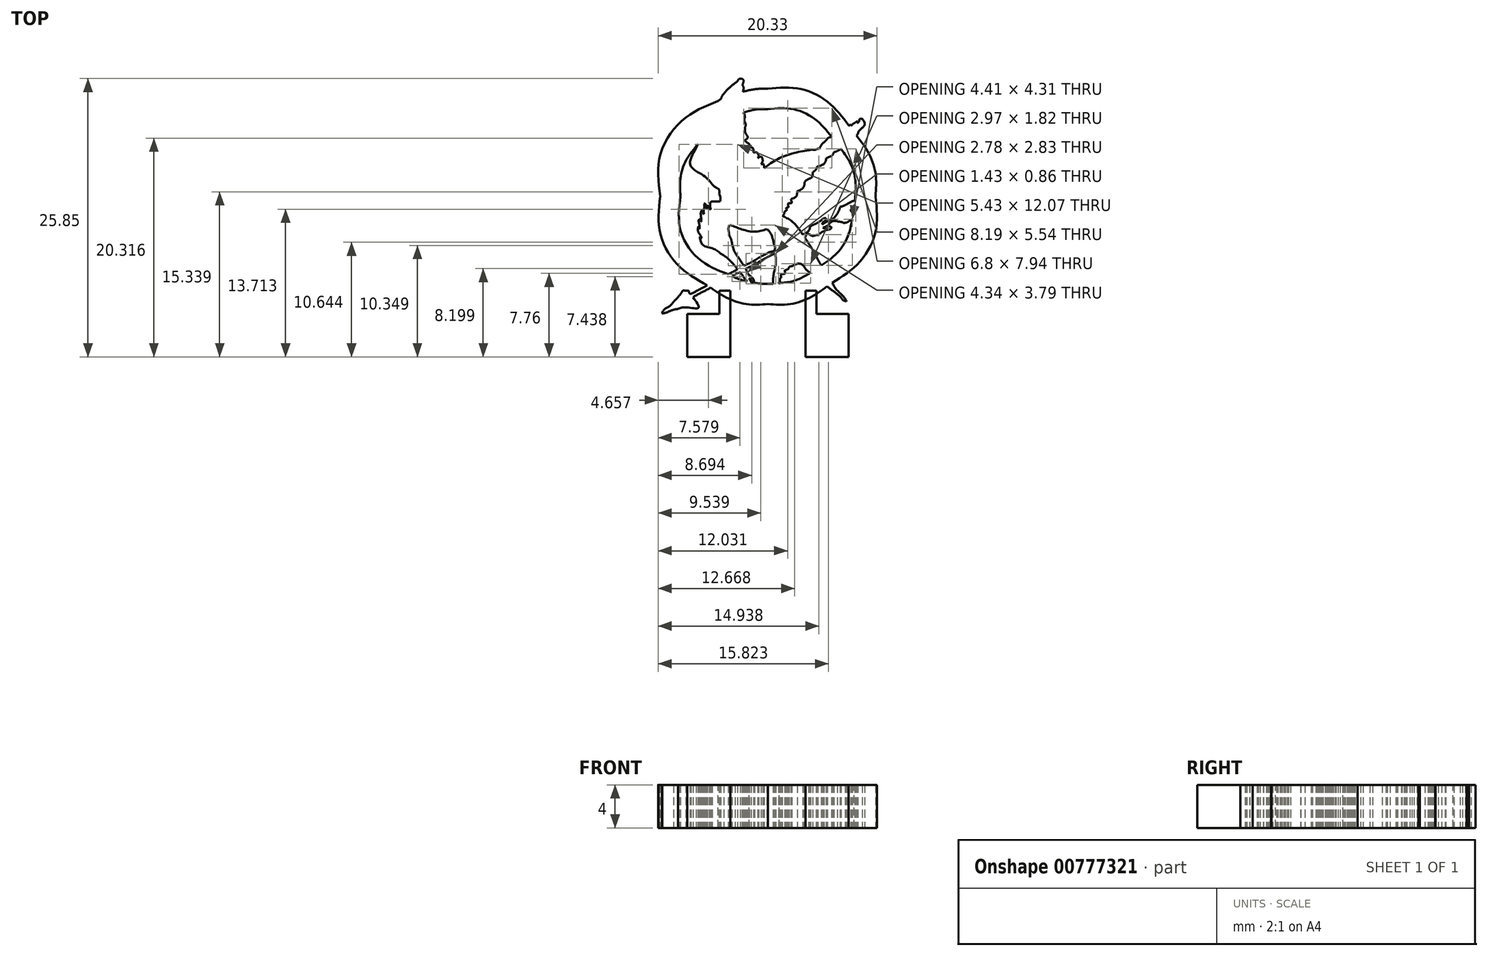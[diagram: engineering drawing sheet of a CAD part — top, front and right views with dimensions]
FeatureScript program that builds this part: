
annotation { "Feature Type Name" : "Feature", "Feature Type Description" : "" }
export const myFeature = defineFeature(function(context is Context, id is Id, definition is map)
    precondition{}
    {
        {
            var Q0;
            Q0=qCreatedBy(makeId("Top.planeOp"),FACE);
            var sketch = newSketch(context, id + "F0", { "sketchPlane" : qUnion([Q0])});
            skFitSpline(sketch, "E0", {"points": [v(6.8, 4.37) * mm, v(7.63, 3.1) * mm, v(8.11, 1.58) * mm, v(8.11, -0.04) * mm]});
            skFitSpline(sketch, "E1", {"points": [v(8.11, -0.04) * mm, v(8.11, -0.15) * mm, v(8.11, -0.27) * mm, v(8.1, -0.38) * mm]});
            skFitSpline(sketch, "E2", {"points": [v(8.08, -0.82) * mm, v(8.06, -1.02) * mm, v(8.03, -1.22) * mm, v(8, -1.41) * mm]});
            skFitSpline(sketch, "E3", {"points": [v(7.84, -2.14) * mm, v(7.37, -3.87) * mm, v(6.35, -5.38) * mm, v(4.97, -6.45) * mm]});
            skFitSpline(sketch, "E4", {"points": [v(5.98, -8.05) * mm, v(8.42, -6.23) * mm, v(10, -3.32) * mm, v(10, -0.04) * mm]});
            skFitSpline(sketch, "E5", {"points": [v(10, -0.04) * mm, v(10, 2.06) * mm, v(9.35, 4) * mm, v(8.24, 5.62) * mm]});
            skFitSpline(sketch, "E6", {"points": [v(3.96, -7.12) * mm, v(3.06, -7.62) * mm, v(2.06, -7.96) * mm, v(1, -8.1) * mm]});
            skFitSpline(sketch, "E7", {"points": [v(0.47, -8.14) * mm, v(0.31, -8.15) * mm, v(0.16, -8.16) * mm, v(0, -8.16) * mm]});
            skFitSpline(sketch, "E8", {"points": [v(0, -8.16) * mm, v(-0.42, -8.16) * mm, v(-0.84, -8.12) * mm, v(-1.25, -8.06) * mm]});
            skFitSpline(sketch, "E9", {"points": [v(-1.32, -8.05) * mm, v(-1.4, -8.03) * mm, v(-1.48, -8.02) * mm, v(-1.56, -8) * mm]});
            skFitSpline(sketch, "E10", {"points": [v(-1.9, -7.93) * mm, v(-2.4, -7.81) * mm, v(-2.87, -7.65) * mm, v(-3.33, -7.44) * mm]});
            skFitSpline(sketch, "E11", {"points": [v(-5.28, -8.5) * mm, v(-5.29, -8.5) * mm, v(-5.3, -8.5) * mm, v(-5.3, -8.51) * mm]});
            skFitSpline(sketch, "E12", {"points": [v(-5.3, -8.51) * mm, v(-3.77, -9.48) * mm, v(-1.95, -10.04) * mm, v(0, -10.04) * mm]});
            skFitSpline(sketch, "E13", {"points": [v(0, -10.04) * mm, v(2.03, -10.04) * mm, v(3.92, -9.43) * mm, v(5.5, -8.39) * mm]});
            skFitSpline(sketch, "E14", {"points": [v(-3.7, -7.26) * mm, v(-6.32, -5.92) * mm, v(-8.11, -3.19) * mm, v(-8.11, -0.04) * mm]});
            skFitSpline(sketch, "E15", {"points": [v(-8.11, -0.04) * mm, v(-8.11, 1.78) * mm, v(-7.51, 3.45) * mm, v(-6.5, 4.8) * mm]});
            skFitSpline(sketch, "E16", {"points": [v(-4.63, 8.82) * mm, v(-7.82, 7.15) * mm, v(-10, 3.8) * mm, v(-10, -0.04) * mm]});
            skFitSpline(sketch, "E17", {"points": [v(-10, -0.04) * mm, v(-10, -3.47) * mm, v(-8.27, -6.5) * mm, v(-5.63, -8.3) * mm]});
            skFitSpline(sketch, "E18", {"points": [v(-2.25, 7.75) * mm, v(-1.54, 7.96) * mm, v(-0.78, 8.07) * mm, v(0, 8.07) * mm]});
            skFitSpline(sketch, "E19", {"points": [v(0, 8.07) * mm, v(2.34, 8.07) * mm, v(4.45, 7.08) * mm, v(5.94, 5.48) * mm]});
            skFitSpline(sketch, "E20", {"points": [v(7.52, 6.54) * mm, v(5.69, 8.63) * mm, v(3, 9.96) * mm, v(0, 9.96) * mm]});
            skFitSpline(sketch, "E21", {"points": [v(0, 9.96) * mm, v(-0.8, 9.96) * mm, v(-1.57, 9.86) * mm, v(-2.31, 9.69) * mm]});
            skFitSpline(sketch, "E22", {"points": [v(-3.62, -3.38) * mm, v(-3.67, -3.09) * mm, v(-3.61, -2.8) * mm, v(-3.43, -2.7) * mm]});
            skFitSpline(sketch, "E23", {"points": [v(-3.43, -2.7) * mm, v(-2.55, -3.05) * mm, v(-1.27, -3.3) * mm, v(-0.1, -3.08) * mm]});
            skFitSpline(sketch, "E24", {"points": [v(-0.1, -3.08) * mm, v(0.21, -3.38) * mm, v(0.4, -3.81) * mm, v(0.54, -4.38) * mm]});
            skFitSpline(sketch, "E25", {"points": [v(0.54, -4.38) * mm, v(0.58, -4.53) * mm, v(0.68, -4.8) * mm, v(0.64, -4.92) * mm]});
            skFitSpline(sketch, "E26", {"points": [v(0.64, -4.92) * mm, v(0.58, -5.08) * mm, v(0.12, -5.22) * mm, v(-0.07, -5.32) * mm]});
            skFitSpline(sketch, "E27", {"points": [v(-0.07, -5.32) * mm, v(-0.77, -5.7) * mm, v(-1.6, -6.18) * mm, v(-2.25, -6.48) * mm]});
            skFitSpline(sketch, "E28", {"points": [v(-2.25, -6.48) * mm, v(-2.6, -5.92) * mm, v(-3.14, -5.07) * mm, v(-3.36, -4.24) * mm]});
            skFitSpline(sketch, "E29", {"points": [v(-3.36, -4.24) * mm, v(-3.44, -3.94) * mm, v(-3.59, -3.63) * mm, v(-3.62, -3.38) * mm]});
            skFitSpline(sketch, "E30", {"points": [v(8, -1.41) * mm, v(7.9, -1.43) * mm, v(7.8, -1.44) * mm, v(7.76, -1.44) * mm]});
            skFitSpline(sketch, "E31", {"points": [v(7.76, -1.44) * mm, v(7.73, -1.41) * mm, v(7.75, -1.33) * mm, v(7.69, -1.33) * mm]});
            skFitSpline(sketch, "E32", {"points": [v(7.69, -1.33) * mm, v(7.79, -1.13) * mm, v(7.93, -0.97) * mm, v(8.08, -0.82) * mm]});
            skFitSpline(sketch, "E33", {"points": [v(8.1, -0.38) * mm, v(7.64, -0.59) * mm, v(7.2, -0.83) * mm, v(6.72, -1.02) * mm]});
            skFitSpline(sketch, "E34", {"points": [v(6.72, -1.02) * mm, v(6.57, -1.41) * mm, v(6.37, -1.75) * mm, v(6.13, -2.06) * mm]});
            skFitSpline(sketch, "E35", {"points": [v(6.13, -2.06) * mm, v(5.76, -2.24) * mm, v(5.4, -2.42) * mm, v(5.06, -2.63) * mm]});
            skFitSpline(sketch, "E36", {"points": [v(5.06, -2.63) * mm, v(5.1, -2.45) * mm, v(5.35, -2.28) * mm, v(5.42, -2.06) * mm]});
            skFitSpline(sketch, "E37", {"points": [v(5.42, -2.06) * mm, v(5.14, -2.1) * mm, v(4.9, -2.31) * mm, v(4.64, -2.46) * mm]});
            skFitSpline(sketch, "E38", {"points": [v(4.64, -2.46) * mm, v(4.38, -2.6) * mm, v(4.1, -2.73) * mm, v(3.88, -2.91) * mm]});
            skFitSpline(sketch, "E39", {"points": [v(3.88, -2.91) * mm, v(3.88, -3.08) * mm, v(3.8, -3.15) * mm, v(3.78, -3.29) * mm]});
            skFitSpline(sketch, "E40", {"points": [v(3.78, -3.29) * mm, v(3.6, -3.39) * mm, v(3.43, -3.49) * mm, v(3.24, -3.57) * mm]});
            skFitSpline(sketch, "E41", {"points": [v(3.24, -3.57) * mm, v(2.74, -2.87) * mm, v(2.13, -2.27) * mm, v(1.35, -1.85) * mm]});
            skFitSpline(sketch, "E42", {"points": [v(1.35, -1.85) * mm, v(1.49, -1.7) * mm, v(1.55, -1.48) * mm, v(1.7, -1.35) * mm]});
            skFitSpline(sketch, "E43", {"points": [v(1.7, -1.35) * mm, v(1.74, -1.3) * mm, v(1.73, -1.2) * mm, v(1.68, -1.18) * mm]});
            skFitSpline(sketch, "E44", {"points": [v(1.68, -1.18) * mm, v(1.73, -1.1) * mm, v(1.85, -1.07) * mm, v(1.92, -1) * mm]});
            skFitSpline(sketch, "E45", {"points": [v(1.92, -1) * mm, v(1.9, -0.67) * mm, v(2.19, -0.65) * mm, v(2.13, -0.28) * mm]});
            skFitSpline(sketch, "E46", {"points": [v(2.13, -0.28) * mm, v(2.45, -0.16) * mm, v(2.67, 0.06) * mm, v(2.72, 0.45) * mm]});
            skFitSpline(sketch, "E47", {"points": [v(2.72, 0.45) * mm, v(3.1, 0.6) * mm, v(3.34, 0.9) * mm, v(3.43, 1.35) * mm]});
            skFitSpline(sketch, "E48", {"points": [v(3.43, 1.35) * mm, v(3.74, 1.57) * mm, v(4.1, 1.76) * mm, v(4.16, 2.23) * mm]});
            skFitSpline(sketch, "E49", {"points": [v(4.16, 2.23) * mm, v(4.35, 2.34) * mm, v(4.49, 2.5) * mm, v(4.56, 2.72) * mm]});
            skFitSpline(sketch, "E50", {"points": [v(4.56, 2.72) * mm, v(4.97, 2.86) * mm, v(5.3, 3.08) * mm, v(5.42, 3.5) * mm]});
            skFitSpline(sketch, "E51", {"points": [v(5.42, 3.5) * mm, v(5.71, 3.64) * mm, v(5.99, 3.79) * mm, v(6.13, 4.07) * mm]});
            skFitSpline(sketch, "E52", {"points": [v(6.13, 4.07) * mm, v(6.3, 4.13) * mm, v(6.58, 4.26) * mm, v(6.8, 4.37) * mm]});
            skFitSpline(sketch, "E53", {"points": [v(8.33, 5.73) * mm, v(8.55, 6.15) * mm, v(8.98, 6.6) * mm, v(8.78, 7.17) * mm]});
            skFitSpline(sketch, "E54", {"points": [v(8.78, 7.17) * mm, v(8.53, 7.15) * mm, v(8.47, 6.94) * mm, v(8.35, 6.8) * mm]});
            skFitSpline(sketch, "E55", {"points": [v(8.35, 6.8) * mm, v(8.3, 6.83) * mm, v(8.3, 6.92) * mm, v(8.19, 6.89) * mm]});
            skFitSpline(sketch, "E56", {"points": [v(8.19, 6.89) * mm, v(8.02, 6.77) * mm, v(7.85, 6.65) * mm, v(7.71, 6.5) * mm]});
            skFitSpline(sketch, "E57", {"points": [v(7.71, 6.5) * mm, v(7.7, 6.61) * mm, v(7.57, 6.56) * mm, v(7.52, 6.54) * mm]});
            skLineSegment(sketch, "E58", {"start": v(8.24, 5.62) * mm, "end": v(8.33, 5.73) * mm});
            skFitSpline(sketch, "E59", {"points": [v(5.94, 5.48) * mm, v(5.63, 5.42) * mm, v(5.43, 5.2) * mm, v(5.2, 5) * mm]});
            skFitSpline(sketch, "E60", {"points": [v(5.2, 5) * mm, v(5, 4.8) * mm, v(4.8, 4.48) * mm, v(4.56, 4.38) * mm]});
            skFitSpline(sketch, "E61", {"points": [v(4.56, 4.38) * mm, v(4.38, 4.3) * mm, v(4.08, 4.3) * mm, v(3.83, 4.26) * mm]});
            skFitSpline(sketch, "E62", {"points": [v(3.83, 4.26) * mm, v(2.27, 3.96) * mm, v(0.79, 3.37) * mm, v(-0.33, 2.6) * mm]});
            skFitSpline(sketch, "E63", {"points": [v(-0.33, 2.6) * mm, v(-0.36, 2.8) * mm, v(-0.41, 2.96) * mm, v(-0.64, 2.96) * mm]});
            skFitSpline(sketch, "E64", {"points": [v(-0.64, 2.96) * mm, v(-0.5, 3.21) * mm, v(-0.6, 3.65) * mm, v(-0.95, 3.53) * mm]});
            skFitSpline(sketch, "E65", {"points": [v(-0.95, 3.53) * mm, v(-0.87, 3.8) * mm, v(-1.1, 4.07) * mm, v(-1.33, 4.02) * mm]});
            skFitSpline(sketch, "E66", {"points": [v(-1.33, 4.02) * mm, v(-1.34, 4.3) * mm, v(-1.45, 4.5) * mm, v(-1.8, 4.45) * mm]});
            skFitSpline(sketch, "E67", {"points": [v(-1.8, 4.45) * mm, v(-1.71, 4.8) * mm, v(-1.97, 5) * mm, v(-2.13, 5.18) * mm]});
            skFitSpline(sketch, "E68", {"points": [v(-2.13, 5.18) * mm, v(-1.87, 5.47) * mm, v(-2.07, 5.84) * mm, v(-2.1, 6.2) * mm]});
            skFitSpline(sketch, "E69", {"points": [v(-2.1, 6.2) * mm, v(-2.13, 6.38) * mm, v(-2.06, 6.56) * mm, v(-2.09, 6.74) * mm]});
            skFitSpline(sketch, "E70", {"points": [v(-2.09, 6.74) * mm, v(-2.1, 6.83) * mm, v(-2.17, 6.92) * mm, v(-2.18, 7) * mm]});
            skFitSpline(sketch, "E71", {"points": [v(-2.18, 7) * mm, v(-2.2, 7.15) * mm, v(-2.14, 7.31) * mm, v(-2.16, 7.45) * mm]});
            skFitSpline(sketch, "E72", {"points": [v(-2.16, 7.45) * mm, v(-2.17, 7.58) * mm, v(-2.24, 7.66) * mm, v(-2.25, 7.75) * mm]});
            skFitSpline(sketch, "E73", {"points": [v(-2.3, 9.75) * mm, v(-2.26, 9.96) * mm, v(-2.27, 10.15) * mm, v(-2.37, 10.3) * mm]});
            skFitSpline(sketch, "E74", {"points": [v(-2.37, 10.3) * mm, v(-2.3, 10.5) * mm, v(-2.27, 10.77) * mm, v(-2.42, 10.9) * mm]});
            skFitSpline(sketch, "E75", {"points": [v(-2.42, 10.9) * mm, v(-2.68, 10.87) * mm, v(-2.84, 10.66) * mm, v(-3.03, 10.5) * mm]});
            skFitSpline(sketch, "E76", {"points": [v(-3.03, 10.5) * mm, v(-3.42, 10.2) * mm, v(-3.78, 9.86) * mm, v(-4.1, 9.5) * mm]});
            skFitSpline(sketch, "E77", {"points": [v(-4.1, 9.5) * mm, v(-4.25, 9.3) * mm, v(-4.37, 9.04) * mm, v(-4.55, 8.9) * mm]});
            skFitSpline(sketch, "E78", {"points": [v(-4.55, 8.9) * mm, v(-4.58, 8.87) * mm, v(-4.6, 8.85) * mm, v(-4.63, 8.82) * mm]});
            skFitSpline(sketch, "E79", {"points": [v(-6.5, 4.8) * mm, v(-6.55, 4.68) * mm, v(-6.64, 4.54) * mm, v(-6.67, 4.42) * mm]});
            skFitSpline(sketch, "E80", {"points": [v(-6.67, 4.42) * mm, v(-7.2, 2.85) * mm, v(-5.96, 1.89) * mm, v(-5.16, 1.1) * mm]});
            skFitSpline(sketch, "E81", {"points": [v(-5.16, 1.1) * mm, v(-4.92, 0.84) * mm, v(-4.54, 0.6) * mm, v(-4.52, 0.24) * mm]});
            skFitSpline(sketch, "E82", {"points": [v(-4.52, 0.24) * mm, v(-4.48, -0.48) * mm, v(-5.27, -0.53) * mm, v(-5.3, -1.25) * mm]});
            skFitSpline(sketch, "E83", {"points": [v(-5.3, -1.25) * mm, v(-5.44, -1.17) * mm, v(-5.45, -0.98) * mm, v(-5.61, -0.92) * mm]});
            skFitSpline(sketch, "E84", {"points": [v(-5.61, -0.92) * mm, v(-5.7, -0.94) * mm, v(-5.6, -1.07) * mm, v(-5.64, -1.18) * mm]});
            skFitSpline(sketch, "E85", {"points": [v(-5.64, -1.18) * mm, v(-5.75, -1.04) * mm, v(-5.77, -0.8) * mm, v(-5.92, -0.69) * mm]});
            skFitSpline(sketch, "E86", {"points": [v(-5.92, -0.69) * mm, v(-5.9, -1.03) * mm, v(-5.96, -1.3) * mm, v(-5.94, -1.66) * mm]});
            skFitSpline(sketch, "E87", {"points": [v(-5.94, -1.66) * mm, v(-6.05, -1.6) * mm, v(-6, -1.38) * mm, v(-6.06, -1.28) * mm]});
            skFitSpline(sketch, "E88", {"points": [v(-6.06, -1.28) * mm, v(-6.22, -1.5) * mm, v(-6.2, -2.01) * mm, v(-6.18, -2.34) * mm]});
            skFitSpline(sketch, "E89", {"points": [v(-6.18, -2.34) * mm, v(-6.2, -2.38) * mm, v(-6.23, -2.2) * mm, v(-6.23, -2.13) * mm]});
            skFitSpline(sketch, "E90", {"points": [v(-6.23, -2.13) * mm, v(-6.43, -2.24) * mm, v(-6.36, -2.65) * mm, v(-6.34, -2.91) * mm]});
            skFitSpline(sketch, "E91", {"points": [v(-6.34, -2.91) * mm, v(-6.36, -3.03) * mm, v(-6.42, -2.83) * mm, v(-6.46, -2.82) * mm]});
            skFitSpline(sketch, "E92", {"points": [v(-6.46, -2.82) * mm, v(-6.48, -3.3) * mm, v(-6.3, -3.6) * mm, v(-6.13, -3.9) * mm]});
            skFitSpline(sketch, "E93", {"points": [v(-6.13, -3.9) * mm, v(-6.2, -3.88) * mm, v(-6.24, -3.81) * mm, v(-6.32, -3.79) * mm]});
            skFitSpline(sketch, "E94", {"points": [v(-6.32, -3.79) * mm, v(-6, -4.58) * mm, v(-5.09, -4.88) * mm, v(-4.38, -5.35) * mm]});
            skFitSpline(sketch, "E95", {"points": [v(-4.38, -5.35) * mm, v(-3.75, -5.76) * mm, v(-3.27, -6.25) * mm, v(-2.82, -6.8) * mm]});
            skFitSpline(sketch, "E96", {"points": [v(-2.82, -6.8) * mm, v(-3.1, -6.96) * mm, v(-3.4, -7.11) * mm, v(-3.7, -7.26) * mm]});
            skLineSegment(sketch, "E97", {"start": v(-2.31, 9.69) * mm, "end": v(-2.3, 9.75) * mm});
            skFitSpline(sketch, "E98", {"points": [v(-5.63, -8.3) * mm, v(-6, -8.49) * mm, v(-6.75, -8.88) * mm, v(-7.13, -9.09) * mm]});
            skFitSpline(sketch, "E99", {"points": [v(-7.13, -9.09) * mm, v(-7.3, -9.02) * mm, v(-7.34, -8.8) * mm, v(-7.62, -8.8) * mm]});
            skFitSpline(sketch, "E100", {"points": [v(-7.62, -8.8) * mm, v(-7.9, -8.8) * mm, v(-8.05, -9.03) * mm, v(-8.24, -9.25) * mm]});
            skFitSpline(sketch, "E101", {"points": [v(-8.24, -9.25) * mm, v(-8.41, -9.47) * mm, v(-8.61, -9.67) * mm, v(-8.76, -9.82) * mm]});
            skFitSpline(sketch, "E102", {"points": [v(-8.76, -9.82) * mm, v(-9.17, -10.26) * mm, v(-9.6, -10.52) * mm, v(-9.85, -10.9) * mm]});
            skFitSpline(sketch, "E103", {"points": [v(-9.85, -10.9) * mm, v(-9.84, -10.9) * mm, v(-9.83, -10.9) * mm, v(-9.82, -10.9) * mm]});
            skFitSpline(sketch, "E104", {"points": [v(-9.82, -10.9) * mm, v(-9.4, -10.8) * mm, v(-8.94, -10.62) * mm, v(-8.33, -10.48) * mm]});
            skFitSpline(sketch, "E105", {"points": [v(-8.33, -10.48) * mm, v(-7.64, -10.33) * mm, v(-6.45, -10.38) * mm, v(-6.96, -9.4) * mm]});
            skFitSpline(sketch, "E106", {"points": [v(-6.96, -9.4) * mm, v(-6.42, -9.1) * mm, v(-5.86, -8.8) * mm, v(-5.3, -8.51) * mm]});
            skFitSpline(sketch, "E107", {"points": [v(-3.33, -7.44) * mm, v(-3.08, -7.31) * mm, v(-2.76, -7.15) * mm, v(-2.58, -7.07) * mm]});
            skFitSpline(sketch, "E108", {"points": [v(-2.58, -7.07) * mm, v(-2.35, -7.36) * mm, v(-2.16, -7.68) * mm, v(-1.9, -7.93) * mm]});
            skFitSpline(sketch, "E109", {"points": [v(-1.56, -8) * mm, v(-1.62, -7.89) * mm, v(-1.68, -7.77) * mm, v(-1.75, -7.67) * mm]});
            skFitSpline(sketch, "E110", {"points": [v(-1.75, -7.67) * mm, v(-1.61, -7.72) * mm, v(-1.5, -7.93) * mm, v(-1.32, -8.05) * mm]});
            skFitSpline(sketch, "E111", {"points": [v(-1.25, -8.06) * mm, v(-1.46, -7.57) * mm, v(-1.84, -7.24) * mm, v(-2.04, -6.74) * mm]});
            skFitSpline(sketch, "E112", {"points": [v(-2.04, -6.74) * mm, v(-1.1, -6.3) * mm, v(-0.25, -5.77) * mm, v(0.69, -5.32) * mm]});
            skFitSpline(sketch, "E113", {"points": [v(0.69, -5.32) * mm, v(0.72, -6.37) * mm, v(0.55, -7.2) * mm, v(0.47, -8.14) * mm]});
            skFitSpline(sketch, "E114", {"points": [v(1, -8.1) * mm, v(1.01, -8.06) * mm, v(1.03, -8.04) * mm, v(1.04, -8.02) * mm]});
            skFitSpline(sketch, "E115", {"points": [v(1.04, -8.02) * mm, v(1.13, -7.88) * mm, v(1.13, -7.67) * mm, v(1.25, -7.57) * mm]});
            skFitSpline(sketch, "E116", {"points": [v(1.25, -7.57) * mm, v(1.24, -7.24) * mm, v(1.54, -7.22) * mm, v(1.56, -6.9) * mm]});
            skFitSpline(sketch, "E117", {"points": [v(1.56, -6.9) * mm, v(1.74, -6.84) * mm, v(1.9, -6.76) * mm, v(1.96, -6.58) * mm]});
            skFitSpline(sketch, "E118", {"points": [v(1.96, -6.58) * mm, v(2.4, -6.43) * mm, v(2.85, -6.26) * mm, v(3.31, -6.46) * mm]});
            skFitSpline(sketch, "E119", {"points": [v(3.31, -6.46) * mm, v(3.47, -6.73) * mm, v(3.68, -6.96) * mm, v(3.96, -7.12) * mm]});
            skFitSpline(sketch, "E120", {"points": [v(5.54, -8.43) * mm, v(5.82, -8.66) * mm, v(6.14, -8.87) * mm, v(6.44, -9.1) * mm]});
            skFitSpline(sketch, "E121", {"points": [v(6.44, -9.1) * mm, v(6.73, -9.35) * mm, v(6.98, -9.66) * mm, v(7.3, -9.8) * mm]});
            skFitSpline(sketch, "E122", {"points": [v(7.3, -9.8) * mm, v(6.95, -9.25) * mm, v(6.38, -8.7) * mm, v(6, -8.1) * mm]});
            skLineSegment(sketch, "E123", {"start": v(6, -8.1) * mm, "end": v(5.98, -8.05) * mm});
            skFitSpline(sketch, "E124", {"points": [v(4.97, -6.45) * mm, v(4.46, -5.58) * mm, v(3.97, -4.7) * mm, v(3.43, -3.86) * mm]});
            skFitSpline(sketch, "E125", {"points": [v(3.43, -3.86) * mm, v(3.7, -3.52) * mm, v(4.07, -3.68) * mm, v(4.5, -3.62) * mm]});
            skFitSpline(sketch, "E126", {"points": [v(4.5, -3.62) * mm, v(4.72, -3.58) * mm, v(4.97, -3.38) * mm, v(5.2, -3.26) * mm]});
            skFitSpline(sketch, "E127", {"points": [v(5.2, -3.26) * mm, v(5.47, -3.14) * mm, v(5.75, -3.1) * mm, v(5.91, -2.91) * mm]});
            skFitSpline(sketch, "E128", {"points": [v(5.91, -2.91) * mm, v(5.71, -2.81) * mm, v(5.38, -2.97) * mm, v(5.11, -2.96) * mm]});
            skFitSpline(sketch, "E129", {"points": [v(5.11, -2.96) * mm, v(5.6, -2.7) * mm, v(5.94, -2.36) * mm, v(6.77, -2.41) * mm]});
            skFitSpline(sketch, "E130", {"points": [v(6.77, -2.41) * mm, v(6.9, -2.42) * mm, v(7.04, -2.5) * mm, v(7.17, -2.48) * mm]});
            skFitSpline(sketch, "E131", {"points": [v(7.17, -2.48) * mm, v(7.28, -2.47) * mm, v(7.57, -2.3) * mm, v(7.84, -2.14) * mm]});
            skLineSegment(sketch, "E132", {"start": v(5.5, -8.39) * mm, "end": v(5.54, -8.43) * mm});
            skSolve(sketch);
        }
        {
            var Q0;
            Q0=qCreatedBy(makeId("Top.planeOp"),FACE);
            var sketch = newSketch(context, id + "F1", { "sketchPlane" : qUnion([Q0])});
            skLineSegment(sketch, "E133.bottom", {"start": v(-7.5, -10.94) * mm, "end": v(-3.5, -10.94) * mm});
            skLineSegment(sketch, "E133.top", {"start": v(-7.5, -14.94) * mm, "end": v(-3.5, -14.94) * mm});
            skLineSegment(sketch, "E133.left", {"start": v(-7.5, -10.94) * mm, "end": v(-7.5, -14.94) * mm});
            skLineSegment(sketch, "E133.right", {"start": v(-3.5, -10.94) * mm, "end": v(-3.5, -14.94) * mm});
            skLineSegment(sketch, "E134.MirrorCS", {"start": v(7.5, -14.94) * mm, "end": v(3.5, -14.94) * mm});
            skLineSegment(sketch, "E135.MirrorCS", {"start": v(3.5, -10.94) * mm, "end": v(3.5, -14.94) * mm});
            skLineSegment(sketch, "E136.MirrorCS", {"start": v(7.5, -10.94) * mm, "end": v(3.5, -10.94) * mm});
            skLineSegment(sketch, "E137.MirrorCS", {"start": v(7.5, -10.94) * mm, "end": v(7.5, -14.94) * mm});
            skLineSegment(sketch, "E138", {"start": v(-9.83, -10.94) * mm, "end": v(-3.51, -10.94) * mm, "construction": true});
            skLineSegment(sketch, "E139.bottom", {"start": v(-3.5, -11.25) * mm, "end": v(-4.5, -11.25) * mm});
            skLineSegment(sketch, "E139.top", {"start": v(-3.5, -8.78) * mm, "end": v(-4.5, -8.78) * mm});
            skLineSegment(sketch, "E139.left", {"start": v(-3.5, -11.25) * mm, "end": v(-3.5, -8.78) * mm});
            skLineSegment(sketch, "E139.right", {"start": v(-4.5, -11.25) * mm, "end": v(-4.5, -8.78) * mm});
            skLineSegment(sketch, "E140.MirrorCS", {"start": v(3.5, -11.25) * mm, "end": v(3.5, -8.78) * mm});
            skLineSegment(sketch, "E141.MirrorCS", {"start": v(3.5, -11.25) * mm, "end": v(4.5, -11.25) * mm});
            skLineSegment(sketch, "E142.MirrorCS", {"start": v(4.5, -11.25) * mm, "end": v(4.5, -8.78) * mm});
            skLineSegment(sketch, "E143.MirrorCS", {"start": v(3.5, -8.78) * mm, "end": v(4.5, -8.78) * mm});
            skSolve(sketch);
        }
        {
            var Q0;
            Q0=makeQuery(id+"F0.imprint","IMPRINT",FACE,{"disambiguationData":[TD([[makeQuery(id+"F0.imprint","IMPRINT",EDGE,{"derivedFrom":sQuery(id+"F0.wireOp",EDGE,"E0")}),1.0]])]});
            var Q1;
            Q1=qSketchRegion(id+"F1",true);
            extrude(context, id + "F2", {"entities" : qUnion([Q0, Q1]), "endBound" : BoundingType.SYMMETRIC, "depth" : 4 * mm, "offsetDistance" : 25 * mm});
        }
    });
